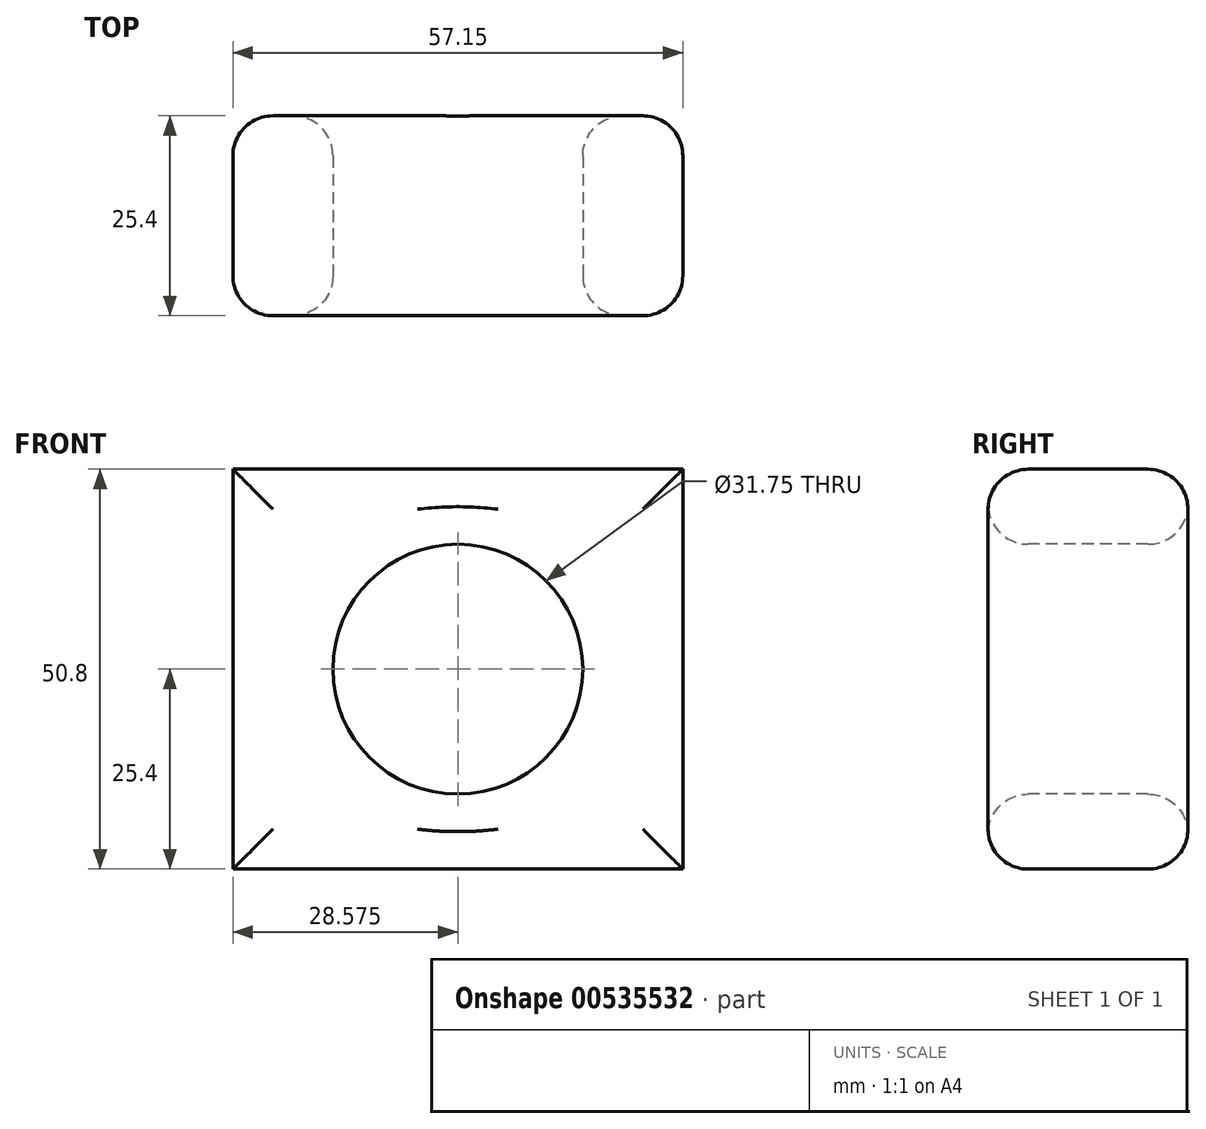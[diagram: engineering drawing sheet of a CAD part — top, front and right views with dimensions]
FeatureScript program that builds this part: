
annotation { "Feature Type Name" : "Feature", "Feature Type Description" : "" }
export const myFeature = defineFeature(function(context is Context, id is Id, definition is map)
    precondition{}
    {
        {
            var Q0;
            Q0=qCreatedBy(makeId("Front.planeOp"),FACE);
            var sketch = newSketch(context, id + "F0", { "sketchPlane" : qUnion([Q0])});
            skLineSegment(sketch, "E0.bottom", {"start": v(0, 0) * mm, "end": v(57.15, 0) * mm});
            skLineSegment(sketch, "E0.top", {"start": v(0, -50.8) * mm, "end": v(57.15, -50.8) * mm});
            skLineSegment(sketch, "E0.left", {"start": v(0, 0) * mm, "end": v(0, -50.8) * mm});
            skLineSegment(sketch, "E0.right", {"start": v(57.15, 0) * mm, "end": v(57.15, -50.8) * mm});
            skSolve(sketch);
        }
        {
            var Q0;
            Q0 = qSketchRegion(id + "F0", true);
            extrude(context, id + "F1", {"entities" : qUnion([Q0]), "depth" : 25.4 * mm, "offsetDistance" : 25.4 * mm});
        }
        {
            var Q0;
            Q0 = qSketchRegion(id + "F0", true);
            extrude(context, id + "F2", {"entities" : qUnion([Q0]), "operationType" : NewBodyOperationType.ADD, "depth" : 25.4 * mm, "offsetDistance" : 25.4 * mm});
        }
        {
            var Q0;
            Q0 = qSketchRegion(id + "F0", true);
            extrude(context, id + "F3", {"entities" : qUnion([Q0]), "operationType" : NewBodyOperationType.ADD, "depth" : 25.4 * mm, "offsetDistance" : 25.4 * mm});
        }
        {
            var Q0;
            Q0=makeQuery(id+"F1.opExtrude","CAP_FACE",FACE,{"disambiguationData":[OSD([sQuery(id+"F0.wireOp",EDGE,"E0.bottom"),sQuery(id+"F0.wireOp",EDGE,"E0.top"),sQuery(id+"F0.wireOp",EDGE,"E0.left"),sQuery(id+"F0.wireOp",EDGE,"E0.right")])],"isStart":false});
            var sketch = newSketch(context, id + "F4", { "sketchPlane" : qUnion([Q0])});
            skCircle(sketch, "E1", {"center": v(28.58, -25.4) * mm, "radius": 15.88 * mm});
            skPoint(sketch, "E1.centerSnap0", {"position": v(0, -25.4) * mm});
            skPoint(sketch, "E1.centerSnap1", {"position": v(28.58, 0) * mm});
            skSolve(sketch);
        }
        {
            var Q0;
            Q0 = qSketchRegion(id + "F4", true);
            extrude(context, id + "F5", {"entities" : qUnion([Q0]), "operationType" : NewBodyOperationType.REMOVE, "oppositeDirection" : true, "depth" : 25.4 * mm, "offsetDistance" : 25.4 * mm});
        }
        {
            var Q0;
            Q0=makeQuery(id+"F1.opExtrude","CAP_FACE",FACE,{"disambiguationData":[OSD([sQuery(id+"F0.wireOp",EDGE,"E0.bottom"),sQuery(id+"F0.wireOp",EDGE,"E0.top"),sQuery(id+"F0.wireOp",EDGE,"E0.left"),sQuery(id+"F0.wireOp",EDGE,"E0.right")])],"isStart":false});
            fillet(context, id + "F6", {"entities" : qUnion([Q0]), "radius" : 5.08 * mm, "tangentPropagation" : true, "allowEdgeOverflow" : false});
        }
        {
            var Q0;
            Q0=makeQuery(id+"F1.opExtrude","CAP_FACE",FACE,{"disambiguationData":[OSD([sQuery(id+"F0.wireOp",EDGE,"E0.bottom"),sQuery(id+"F0.wireOp",EDGE,"E0.top"),sQuery(id+"F0.wireOp",EDGE,"E0.left"),sQuery(id+"F0.wireOp",EDGE,"E0.right")])],"isStart":true});
            fillet(context, id + "F7", {"entities" : qUnion([Q0]), "radius" : 5.08 * mm, "tangentPropagation" : true, "allowEdgeOverflow" : false});
        }
    });
